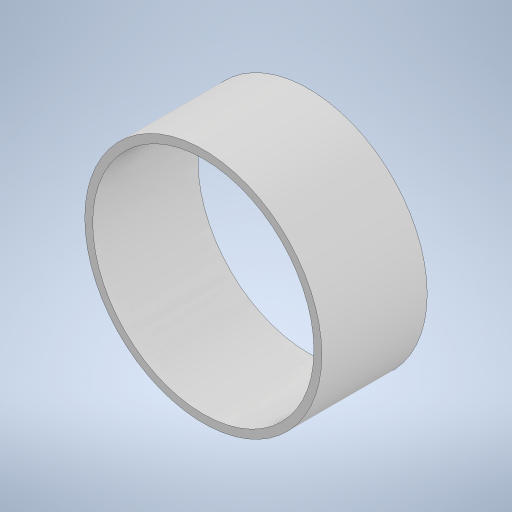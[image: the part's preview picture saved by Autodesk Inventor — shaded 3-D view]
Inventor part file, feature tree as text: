
AUTODESK INVENTOR PART (.ipt)
format: ipt  version: 2024 (Build 280153000, 153)  size: 223,744 bytes
history: native  units: mm
features: extrude x1, sketch x1
ambient origin geometry x8: Origin, YZ Plane, XZ Plane, XY Plane, X Axis, Y Axis, Z Axis, Center Point
bodies: Solid1 (feature_tree)
feature tree (2):
  extrude  "Extrusion1"  Depth=20.0mm
  sketch  "Sketch1"  dims[d0=42.0mm d1=45.0mm d2=20.0mm d3=0.0mm]
